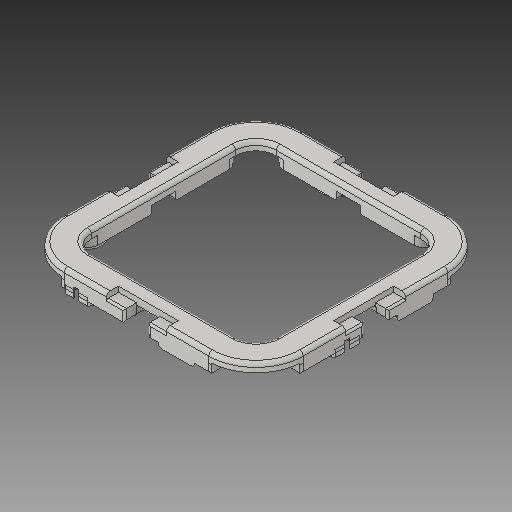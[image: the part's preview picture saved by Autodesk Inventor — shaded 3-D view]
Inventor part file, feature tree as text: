
AUTODESK INVENTOR PART (.ipt)
format: ipt  version: 2018 (Build 220112000, 112)  size: 1,674,752 bytes
history: native  units: in
note: dims shown in document units (in); Inventor stores cm internally (conversion verified against a paired STEP export)
features: extrude x16, other x14, projected_geometry x11, sketch x9, mirror x6, fillet x6, plane x4, thicken_offset x3, pattern_circular x2, emboss x1
ambient origin geometry x8: Origin, YZ Plane, XZ Plane, XY Plane, X Axis, Y Axis, Z Axis, Center Point
bodies: Solid15 (feature_tree), Solid27 (feature_tree), Solid28 (feature_tree), Solid29 (feature_tree), Solid30 (feature_tree), Solid31 (feature_tree), Solid1 (feature_tree)
feature tree (72):
  other  "Remote Shell.ipt"
  other  "Center Axis"
  other  "Top Plane"
  other  "Bottom Plane"
  mirror  "Mirror Split 1"
  mirror  "Mirror Split 2"
  plane  "Work Plane9"
  other  "Magnet Bottom Plane"
  other  "Magnet Sketch"
  extrude  "Magnet Holder"  [1 undecoded]
  other  "Mating Sketch"
  extrude  "Extrusion16"  Depth=0.02in TaperAngle=0.0deg
  extrude  "Extrusion15"  Depth=0.04in
  mirror  "Mirror7"
  pattern_circular  "Circular Pattern9"  [2 undecoded]
  fillet  "Fillet8"  Radius=0.1in
  fillet  "Fillet9"  Radius=0.025in
  fillet  "Fillet10"  Radius=0.025in
  thicken_offset  "Thicken2"
  sketch  "Sketch28"  dims[d60=0.075in d61=0.075in d62=0.03in d63=0.03in d64=0.02in d65=0.0in]
  extrude  "Extrusion19"  Depth=1.5748in TaperAngle=360.0deg
  plane  "Work Plane21"
  extrude  "Extrusion26"  Depth=0.025in
  extrude  "Extrusion31"  Depth=0.0312in
  extrude  "Extrusion36"  Depth=0.06in
  extrude  "Extrusion21"  Depth=0.075in
  mirror  "Mirror9"
  mirror  "Mirror10"
  mirror  "Mirror11"
  plane  "Work Plane19"
  extrude  "Extrusion24"  TaperAngle=0.0deg  [1 undecoded]
  extrude  "Extrusion32"  Depth=0.03in
  plane  "Work Plane23"
  other  "Button Peg Sketch"
  extrude  "Extrusion37"  Depth=0.015in
  extrude  "Extrusion28"  Depth=0.0625in
  extrude  "Extrusion29"  Depth=0.015in
  thicken_offset  "Thicken3"
  other  "Button Paddle Sketch"
  extrude  "Extrusion30"  Depth=1.0in TaperAngle=0.0deg
  pattern_circular  "Circular Pattern14"  [2 undecoded]
  thicken_offset  "Thicken17"
  fillet  "Fillet19"  Radius=0.025in
  emboss  "Emboss5"
  fillet  "Fillet16"  Radius=0.05in
  fillet  "Fillet18"  Radius=0.1in
  sketch  "Sketch40"  dims[d142=0.15in]
  sketch  "Sketch41"  dims[d143=0.025in d144=0.15in d145=-0.2405in d146=0.1in d147=0.0in d149=0.025in d150=0.025in d164=1.5748in d165=360.0deg d167=0.025in d168=0.0312in d209=0.06in d212=0.075in d213=0.0in d214=0.0in d217=0.03in d218=0.015in d219=0.0625in d220=0.1718in d239=0.015in d240=0.04in d241=1.0in d242=0.0in d245=1.0in d246=0.0in d253=0.025in d254=0.0in d261=0.05in d262=0.0in d267=0.1in d268=0.0in d269=1.5748in d270=360.0deg d273=0.05in d274=0.0in d286=0.005in d287=0.0in d290=0.01in d291=0.0in d292=0.6356in d293=1.2197in d300=0.129in d301=0.04in d302=0.025in d303=0.06in d304=0.129in d305=0.04in d306=0.025in d307=0.06in d312=0.129in d313=0.04in d314=0.025in d315=0.06in d320=0.068in d321=0.0in d322=0.025in d324=0.005in d340=0.0625in d341=0.025in d342=0.0in d343=0.03in d344=0.0in d360=0.075in d361=0.075in d362=0.075in d363=0.075in d364=0.075in d365=0.125in d366=0.075in d367=0.125in d370=0.007in d374=0.015in d375=0.01in d376=0.0125in d377=0.075in d378=0.075in d379=0.03in d380=0.03in d381=0.03in d382=0.05in d383=0.05in d384=0.03in d385=0.125in d386=0.04in d387=0.05in d388=135.0deg d389=0.03in d390=0.05in d391=0.03in d392=0.01in d393=0.0in d394=0.01in d395=0.0in d396=135.0deg d397=0.035in d398=0.0125in d399=0.035in d400=0.0125in d401=0.035in d402=0.0125in d403=0.035in d404=0.0125in]
  extrude  "Extrusion38"  Depth=1.5748in TaperAngle=360.0deg
  extrude  "Extrusion39"  Depth=0.05in TaperAngle=0.0deg
  other  "Top Solid::Remote Shell.ipt"
  other  "TaggingFeature1"
  projected_geometry  "Projected Loop3"
  sketch  "Sketch29"  dims[d70=0.129in d71=0.04in]
  other  "Pattern of Solid27:16"
  other  "Pattern of Solid27:17"
  other  "Pattern of Solid29:18"
  sketch  "Sketch31"  dims[d74=0.05in d75=0.0in]
  sketch  "Sketch33"  dims[d78=0.025in]
  projected_geometry  "Projected Loop4"
  projected_geometry  "Projected Loop5"
  projected_geometry  "Projected Loop6"
  projected_geometry  "Projected Loop7"
  projected_geometry  "Projected Loop8"
  projected_geometry  "Projected Loop9"
  projected_geometry  "Projected Loop10"
  projected_geometry  "Projected Loop11"
  sketch  "Sketch38"  dims[d140=0.25in]
  sketch  "Sketch39"  dims[d141=0.12in]
  projected_geometry  "Projected Loop17"
  projected_geometry  "Projected Loop18"
  sketch  "Sketch15"  dims[d0=0.3937in d45=-0.0675in]
note: 6 required parameter values undecoded (feature->parameter linkage not recoverable at this tier; creation-order binding heuristic only, values carry confidence <= 0.55)
